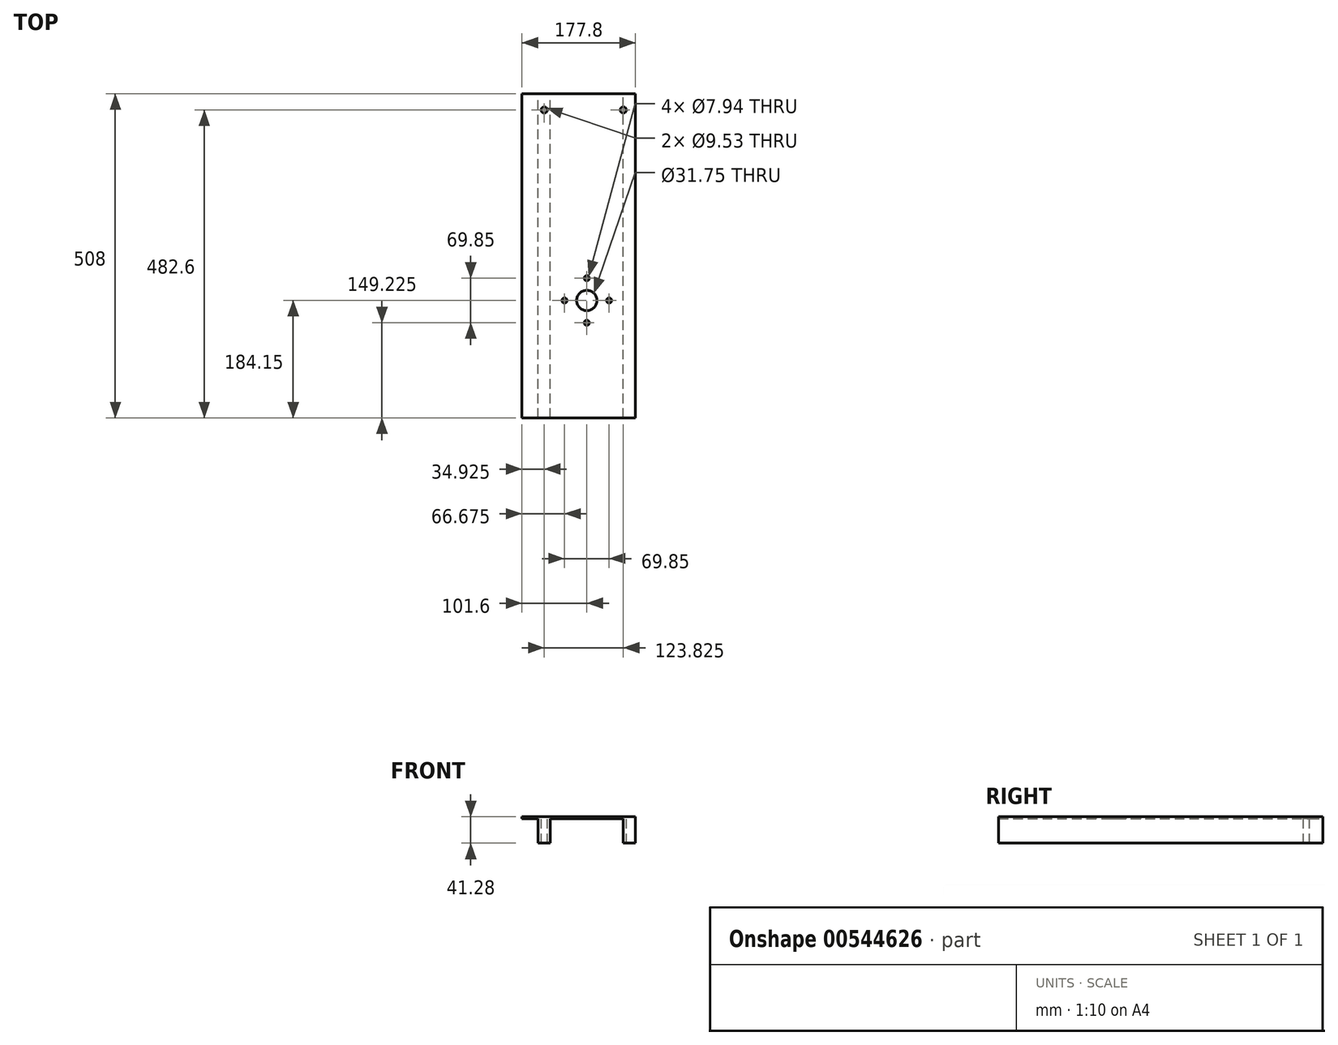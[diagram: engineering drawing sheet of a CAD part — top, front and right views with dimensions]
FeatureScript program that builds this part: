
annotation { "Feature Type Name" : "Feature", "Feature Type Description" : "" }
export const myFeature = defineFeature(function(context is Context, id is Id, definition is map)
    precondition{}
    {
        {
            var Q0;
            Q0=qCreatedBy(makeId("Front.planeOp"),FACE);
            var sketch = newSketch(context, id + "F0", { "sketchPlane" : qUnion([Q0])});
            skLineSegment(sketch, "E0.bottom", {"start": v(0, 0) * mm, "end": v(25.4, 0) * mm});
            skLineSegment(sketch, "E0.top", {"start": v(0, 3.17) * mm, "end": v(177.8, 3.17) * mm});
            skLineSegment(sketch, "E0.left", {"start": v(0, 0) * mm, "end": v(0, 3.17) * mm});
            skLineSegment(sketch, "E0.right", {"start": v(177.8, 0) * mm, "end": v(177.8, 3.17) * mm});
            skLineSegment(sketch, "E1.top", {"start": v(25.4, -38.1) * mm, "end": v(44.45, -38.1) * mm});
            skLineSegment(sketch, "E1.left", {"start": v(25.4, 0) * mm, "end": v(25.4, -38.1) * mm});
            skLineSegment(sketch, "E1.right", {"start": v(44.45, 0) * mm, "end": v(44.45, -38.1) * mm});
            skLineSegment(sketch, "E2.top", {"start": v(158.75, -38.1) * mm, "end": v(177.8, -38.1) * mm});
            skLineSegment(sketch, "E2.left", {"start": v(158.75, 0) * mm, "end": v(158.75, -38.1) * mm});
            skLineSegment(sketch, "E2.right", {"start": v(177.8, 0) * mm, "end": v(177.8, -38.1) * mm});
            skLineSegment(sketch, "E3.trimOffspring", {"start": v(44.45, 0) * mm, "end": v(158.75, 0) * mm});
            skSolve(sketch);
        }
        {
            var Q0;
            Q0=makeQuery(id+"F0.imprint","IMPRINT",FACE,{"disambiguationData":[TD([[makeQuery(id+"F0.imprint","IMPRINT",EDGE,{"derivedFrom":sQuery(id+"F0.wireOp",EDGE,"E0.bottom")}),1.0]])]});
            extrude(context, id + "F1", {"entities" : qUnion([Q0]), "depth" : 508 * mm, "offsetDistance" : 25.4 * mm});
        }
        {
            var Q0;
            Q0=makeQuery(id+"F1.opExtrude","SWEPT_FACE",FACE,{"disambiguationData":[OSD([sQuery(id+"F0.wireOp",EDGE,"E0.top")])]});
            var sketch = newSketch(context, id + "F2", { "sketchPlane" : qUnion([Q0])});
            skPoint(sketch, "E4", {"position": v(101.6, -323.85) * mm});
            skSolve(sketch);
        }
        {
            var Q0;
            Q0=sQuery(id+"F2.wireOp",VERTEX,"E4");
            var Q1;
            Q1=makeQuery(id+"F1.opExtrude","SWEPT_BODY",BODY,{"disambiguationData":[OSD([sQuery(id+"F0.wireOp",EDGE,"E0.bottom"),sQuery(id+"F0.wireOp",EDGE,"E0.top"),sQuery(id+"F0.wireOp",EDGE,"E0.left"),sQuery(id+"F0.wireOp",EDGE,"E0.right"),sQuery(id+"F0.wireOp",EDGE,"E1.top"),sQuery(id+"F0.wireOp",EDGE,"E1.left"),sQuery(id+"F0.wireOp",EDGE,"E1.right"),sQuery(id+"F0.wireOp",EDGE,"E2.top"),sQuery(id+"F0.wireOp",EDGE,"E2.left"),sQuery(id+"F0.wireOp",EDGE,"E2.right"),sQuery(id+"F0.wireOp",EDGE,"E3.trimOffspring")])]});
            hole(context, id + "F3", {"style" : HoleStyle.SIMPLE, "endStyle" : HoleEndStyle.THROUGH, "holeDiameter" : 31.75 * mm, "majorDiameter" : 6.35 * mm, "isTappedThrough" : true, "tappedDepth" : 12.7 * mm, "tapClearance" : 3, "locations" : qUnion([Q0]), "scope" : qUnion([Q1])});
        }
        {
            var Q0;
            Q0=makeQuery(id+"F1.opExtrude","SWEPT_FACE",FACE,{"disambiguationData":[OSD([sQuery(id+"F0.wireOp",EDGE,"E0.top")])]});
            var sketch = newSketch(context, id + "F4", { "sketchPlane" : qUnion([Q0])});
            skCircle(sketch, "E5", {"center": v(101.6, -323.85) * mm, "radius": 34.93 * mm, "construction": true});
            skPoint(sketch, "E6", {"position": v(66.68, -323.85) * mm});
            skPoint(sketch, "E7", {"position": v(101.6, -358.77) * mm});
            skPoint(sketch, "E8", {"position": v(136.53, -323.85) * mm});
            skPoint(sketch, "E9", {"position": v(101.6, -288.93) * mm});
            skLineSegment(sketch, "E10", {"start": v(101.6, -358.77) * mm, "end": v(101.6, -288.93) * mm, "construction": true});
            skLineSegment(sketch, "E11", {"start": v(136.53, -323.85) * mm, "end": v(66.68, -323.85) * mm, "construction": true});
            skSolve(sketch);
        }
        {
            var Q0;
            Q0=sQuery(id+"F4.wireOp",VERTEX,"E9");
            var Q1;
            Q1=sQuery(id+"F4.wireOp",VERTEX,"E8");
            var Q2;
            Q2=sQuery(id+"F4.wireOp",VERTEX,"E7");
            var Q3;
            Q3=sQuery(id+"F4.wireOp",VERTEX,"E6");
            var Q4;
            Q4=makeQuery(id+"F1.opExtrude","SWEPT_BODY",BODY,{"disambiguationData":[OSD([sQuery(id+"F0.wireOp",EDGE,"E0.bottom"),sQuery(id+"F0.wireOp",EDGE,"E0.top"),sQuery(id+"F0.wireOp",EDGE,"E0.left"),sQuery(id+"F0.wireOp",EDGE,"E0.right"),sQuery(id+"F0.wireOp",EDGE,"E1.top"),sQuery(id+"F0.wireOp",EDGE,"E1.left"),sQuery(id+"F0.wireOp",EDGE,"E1.right"),sQuery(id+"F0.wireOp",EDGE,"E2.top"),sQuery(id+"F0.wireOp",EDGE,"E2.left"),sQuery(id+"F0.wireOp",EDGE,"E2.right"),sQuery(id+"F0.wireOp",EDGE,"E3.trimOffspring")])]});
            hole(context, id + "F5", {"style" : HoleStyle.SIMPLE, "endStyle" : HoleEndStyle.THROUGH, "holeDiameter" : 7.94 * mm, "majorDiameter" : 6.35 * mm, "isTappedThrough" : true, "tappedDepth" : 12.7 * mm, "tapClearance" : 3, "locations" : qUnion([Q0, Q1, Q2, Q3]), "scope" : qUnion([Q4])});
        }
        {
            var Q0;
            Q0=makeQuery(id+"F1.opExtrude","SWEPT_FACE",FACE,{"disambiguationData":[OSD([sQuery(id+"F0.wireOp",EDGE,"E0.top")])]});
            var sketch = newSketch(context, id + "F6", { "sketchPlane" : qUnion([Q0])});
            skPoint(sketch, "E12", {"position": v(34.93, -25.4) * mm});
            skPoint(sketch, "E13", {"position": v(158.75, -25.4) * mm});
            skSolve(sketch);
        }
        {
            var Q0;
            Q0=sQuery(id+"F6.wireOp",VERTEX,"E12");
            var Q1;
            Q1=sQuery(id+"F6.wireOp",VERTEX,"E13");
            var Q2;
            Q2=makeQuery(id+"F1.opExtrude","SWEPT_BODY",BODY,{"disambiguationData":[OSD([sQuery(id+"F0.wireOp",EDGE,"E0.bottom"),sQuery(id+"F0.wireOp",EDGE,"E0.top"),sQuery(id+"F0.wireOp",EDGE,"E0.left"),sQuery(id+"F0.wireOp",EDGE,"E0.right"),sQuery(id+"F0.wireOp",EDGE,"E1.top"),sQuery(id+"F0.wireOp",EDGE,"E1.left"),sQuery(id+"F0.wireOp",EDGE,"E1.right"),sQuery(id+"F0.wireOp",EDGE,"E2.top"),sQuery(id+"F0.wireOp",EDGE,"E2.left"),sQuery(id+"F0.wireOp",EDGE,"E2.right"),sQuery(id+"F0.wireOp",EDGE,"E3.trimOffspring")])]});
            hole(context, id + "F7", {"style" : HoleStyle.SIMPLE, "endStyle" : HoleEndStyle.THROUGH, "holeDiameter" : 9.52 * mm, "majorDiameter" : 6.35 * mm, "isTappedThrough" : true, "tappedDepth" : 12.7 * mm, "tapClearance" : 3, "locations" : qUnion([Q0, Q1]), "scope" : qUnion([Q2])});
        }
    });
